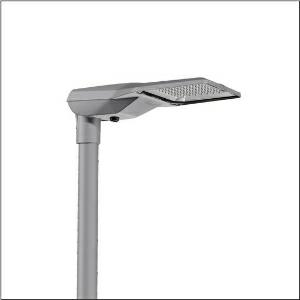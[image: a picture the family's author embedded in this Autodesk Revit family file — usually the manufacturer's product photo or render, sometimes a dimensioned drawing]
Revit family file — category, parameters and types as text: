
# Revit family: streetlight_sl_21_iq_midi___p0_8ab_5xe3r31u08mb_57c5
name_source: partatom
category: Lighting Fixtures
units: mm (PartAtom-declared; Revit-internal decimal feet)

## family parameters
Cut with Voids When Loaded = No
Host = Face
Light Source = No
Part Type = Normal
Room Calculation Point = No
Round Connector Dimension = Use Diameter
Shared = No

## types (1)
- --- (1 x LED, 15920 lm, 129.3 W, 3000K)
    Apparent Load = 129 VA
    CIE Flux Codes = 36 71 98 100 100
    Color Rendering = 70
    Color Temperature = 3000K
    Default Elevation = 1800 mm
    Description = Streetlight SL 21 iQ midi, mast luminaire, primary light control with lens, of PMMA, primary optical cover: cover, of toughened safety glass, transparent, light distribution: P0.8aB, light emission: direct distribution, primary light characteristic: asymmetric, installation type: post-top, side-entry, LED, High Power LED, rated luminous flux: 15.920lm, luminous efficacy: 123lm/W, light colour: 730, colour temperature: 3000K, control gear: iQ-Street Remote, D4i with power reduction, control: pre-setting: logarithmic dimming characteristic, Street-Remote, Auto-Match, Temp-Guard, Lumen-Switch, Night-Set, Smart-Wire, Light-Fading, Desk-Remote (wireless, voltage-free reading and setting of iQ features in the workshop via application-optimized NFC function/RFID function), optimised constant luminous flux control (CLO 2.0), mains connection: 230..240V, AC, 50/60Hz, start of lifetime: 129W, end of service life: 142W, reduction: 56W, luminaire housing, of diecast aluminium, powder-coated, SITECO metallic grey (DB 702S), corrosivity category C5 high according to DIN EN ISO 12944, please order mast flange separately, inclination adjustable: 0°, 5°, 10°, 15°, sealing non-destructively replaceable, multi-level sealing system, length: 644mm, width: 335mm, height: 110mm, mast flange for spigot size: 42mm (side-entry): 5XC10008XM4, 60/48mm (side-entry/post-top): 5XC10108XM2, 76/60mm (side-entry/post-top): 5XC10108XM1, mounting height: 4..8m, Smart Interface below, protection rating (complete): IP66, insulation class (complete): insulation class II (safety insulation), certification: CE, ENEC, ENEC+, VDE, impact resistance: IK10, permissible operating ambient temperature for outdoor applications: -40..+50°C, standard-compliant lighting for roads and squares, packaging unit: 1 piece

Light Distribution: P0.8aB
    Height = 111 mm
    Lamp = 1 x LED
    Lamp Light Flux = 15920 lm
    Lamp Power = 129.3 W
    Lamp count = 1
    Length = 644 mm
    Luminous efficacy = 123 lm/W
    Manufacturer = Siteco
    ModVariant = No
    Model = 5XE3R31U08MB
    Number of Poles = 1
    OnlyDefault = Yes
    Power Factor = 1
    Product Name = Streetlight SL 21 iQ midi | P0.8aB
    Product group = mast luminaire | pylon top
    ProductGroupID = 6100
    Protection Class = Protection class II
    Protection Degree = IP 66
    RLX_Detail_Level = 1
    RLX_Emergency_Light_Flux = 0 lm
    RLX_Emergency_Type = 0
    RLX_Emergency_Type_DB = No
    RlxData = <blob elided: 90981 chars, md5=3a6e2751>
    Socket = socket
    Standby Power = 0 W
    System Light Flux = 15919 lm
    System Power = 129 W
    Type Comments = factory setting: luminous flux: 100 % | dim-lin: 254 | 672 mA
    Type Image = l_1004300.jpg
    URL = http://relux.com
    VarID = @adj_083013
    Voltage = 0 V
    Weight = 0.00 kg
    Width = 336 mm

## geometry (parser evidence)
native form markers: Blend x4, Sweep x11
no freeform markers — native parametric forms only
